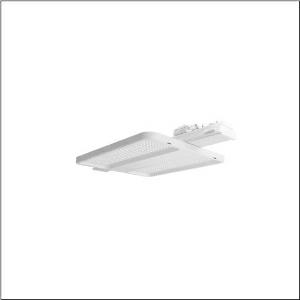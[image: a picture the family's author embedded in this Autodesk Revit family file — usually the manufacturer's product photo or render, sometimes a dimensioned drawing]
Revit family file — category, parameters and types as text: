
# Revit family: highbay_21_fur_licross_r__tragschiene_midi_52hn12da4fla_3db5
name_source: partatom
category: Lighting Fixtures
units: mm (PartAtom-declared; Revit-internal decimal feet)

## family parameters
Cut with Voids When Loaded = No
Host = Face
Light Source = No
Part Type = Normal
Room Calculation Point = No
Round Connector Dimension = Use Diameter
Shared = No

## types (1)
- --- (1 x LED, 14000 lm, 72.1 W, 4000K)
    Apparent Load = 72 VA
    CIE Flux Codes = 90 98 100 100 100
    Color Rendering = 80
    Color Temperature = 4000K
    Default Elevation = 1800 mm
    Description = Highbay 21 for Licross® trunking rail midi, high bay luminaire, primary light control with lens, of PMMA, primary optical cover: cover, of PMMA, light emission: direct distribution, primary light characteristic: symmetric, LED, rated luminous flux: 14.000lm, luminous efficacy: 194lm/W, light colour: 840, colour temperature: 4000K, control gear: DALI 2, with plug, 5-pole, with phase selection, mains connection: 230..240V, AC, 50/60Hz, rated input power: 72.1W, housing frame, of high-performance plastic PA6, matt traffic white (RAL 9016), length: 750mm, width: 442mm, height: 71mm, lever catch, fixing on rail side, of steel, galvanised, white, blank cover, of PC/ABS, traffic white (RAL 9016), protection rating (complete): IP64, insulation class (complete): insulation class I (protective earthing), certification: CE, ENEC, VDE, UKCA, protection symbol: D, impact resistance: IK07, permissible operating ambient temperature: -40..+55°C, LABS conformity tested according to VDMA 24364:2018-05, corresponds to IFS (International Featured Standards) requirements for safety and quality in the food industry, packaging unit: 1 piece
    Height = 72 mm  [stored 0.23622 ft]
    Lamp = 1 x LED
    Lamp Light Flux = 14000 lm
    Lamp Power = 72.1 W
    Lamp count = 1
    Length = 474 mm
    Luminous efficacy = 194 lm/W
    Manufacturer = Siteco
    ModVariant = No
    Model = 52HN12DA4FLA
    Mounting Place = Ceiling
    Mounting Type = Pendant
    Number of Poles = 1
    OnlyDefault = Yes
    Power Factor = 1
    Product Name = Highbay 21 für Licross® Tragschiene midi
    Product group = high bay luminaire
    ProductGroupID = 901
    Protection Class = Protection class I
    Protection Degree = IP 64
    RLX_Detail_Level = 1
    RLX_Emergency_Light_Flux = 0 lm
    RLX_Emergency_Type = 0
    RLX_Emergency_Type_DB = No
    RlxData = <blob elided: 17657 chars, md5=cade6b37>
    Socket = socket
    Standby Power = 0 W
    System Light Flux = 14000 lm
    System Power = 72 W
    Type Comments = factory setting: luminous flux: 100 % | dim-lin: 254 | 334 mA
    Type Image = l_1363258.jpg
    URL = http://relux.com
    VarID = @adj_000517
    Voltage = 0 V
    Weight = 0.00 kg
    Width = 442 mm

note: [stored X ft] marks values corroborated as IEEE doubles in the binary element streams (Revit-internal decimal feet)

## geometry (parser evidence)
native form markers: Blend x4, Sweep x11
no freeform markers — native parametric forms only
